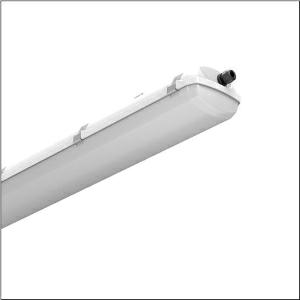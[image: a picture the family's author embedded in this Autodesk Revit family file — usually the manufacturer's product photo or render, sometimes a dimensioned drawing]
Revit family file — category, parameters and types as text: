
# Revit family: monsun_r__ex_51fxa27l460a3g_69c2
name_source: partatom
category: Lighting Fixtures
units: mm (PartAtom-declared; Revit-internal decimal feet)

## family parameters
Cut with Voids When Loaded = No
Host = Face
Light Source = No
Part Type = Normal
Room Calculation Point = No
Round Connector Dimension = Use Diameter
Shared = No

## types (1)
- --- (1 x LED, 6560 lm, 53 W, 4000K)
    Apparent Load = 53 VA
    CIE Flux Codes = 46 76 94 98 100
    Color Rendering = 80
    Color Temperature = 4000K
    Default Elevation = 1800 mm
    Description = Monsun® Ex, damp-proof luminaire, primary optical cover: cover, of PC, UV-stabilised, opal, light emission: direct distribution, primary light characteristic: symmetric, installation type: surface-mounted, LED, rated luminous flux: 6.560lm, luminous efficacy: 124lm/W, light colour: 840, colour temperature: 4000K, control gear: ECG, with terminal, 3+1-pole, max. 2.5mm², through-wiring: 6x 2.5mm², mains connection: 220..250V, AC, 50/60Hz, rated input power: 53W, control gear: single battery element, housing, of PC, light grey (RAL 7035), incl. 1x Ex cable gland M20 for cable diameter 7..12mm with sealing, incl. 1x Ex locking screw M20 with sealing, length: 1.280mm, width: 155mm, height: 105mm, clip for enclosure, of stainless steel, protection rating (complete): IP66, insulation class (complete): insulation class I (protective earthing), certification: CE, explosion class: zone 1,21 II 2G Ex eb mb op is IIC T4 Gb, II 2D Ex tb op is IIIC T67°C Db, impact resistance: IK10, permissible operating ambient temperature: 0..+35°C, contact your sales advisor before using the luminaires in applications with unclear chemical exposure, large temperature fluctuations or condensation-forming humidity, packaging unit: 1 piece
    Height = 105 mm
    Lamp = 1 x LED
    Lamp Light Flux = 6560 lm
    Lamp Power = 53 W
    Lamp count = 1
    Length = 1280 mm
    Luminous efficacy = 124 lm/W
    Manufacturer = Siteco
    ModVariant = No
    Model = 51FXA27L460A3G
    Mounting Place = Ceiling
    Mounting Type = Surface mounted
    Number of Poles = 1
    OnlyDefault = Yes
    Power Factor = 1
    Product Name = Monsun® Ex
    Product group = damp-proof luminaire
    ProductGroupID = 300
    Protection Class = Protection class I
    Protection Degree = IP 66
    RLX_Detail_Level = 1
    RLX_Emergency_Light_Flux = 0 lm
    RLX_Emergency_Type = 0
    RLX_Emergency_Type_DB = No
    RlxData = <blob elided: 41681 chars, md5=42f760a1>
    Socket = socket
    Standby Power = 0 W
    System Light Flux = 6560 lm
    System Power = 53 W
    Type Comments = -
    Type Image = l_1258882.jpg
    URL = http://relux.com
    VarID = @adj_004945
    Voltage = 0 V
    Weight = 0.00 kg
    Width = 155 mm

## geometry (parser evidence)
native form markers: Blend x4, Sweep x10
no freeform markers — native parametric forms only
